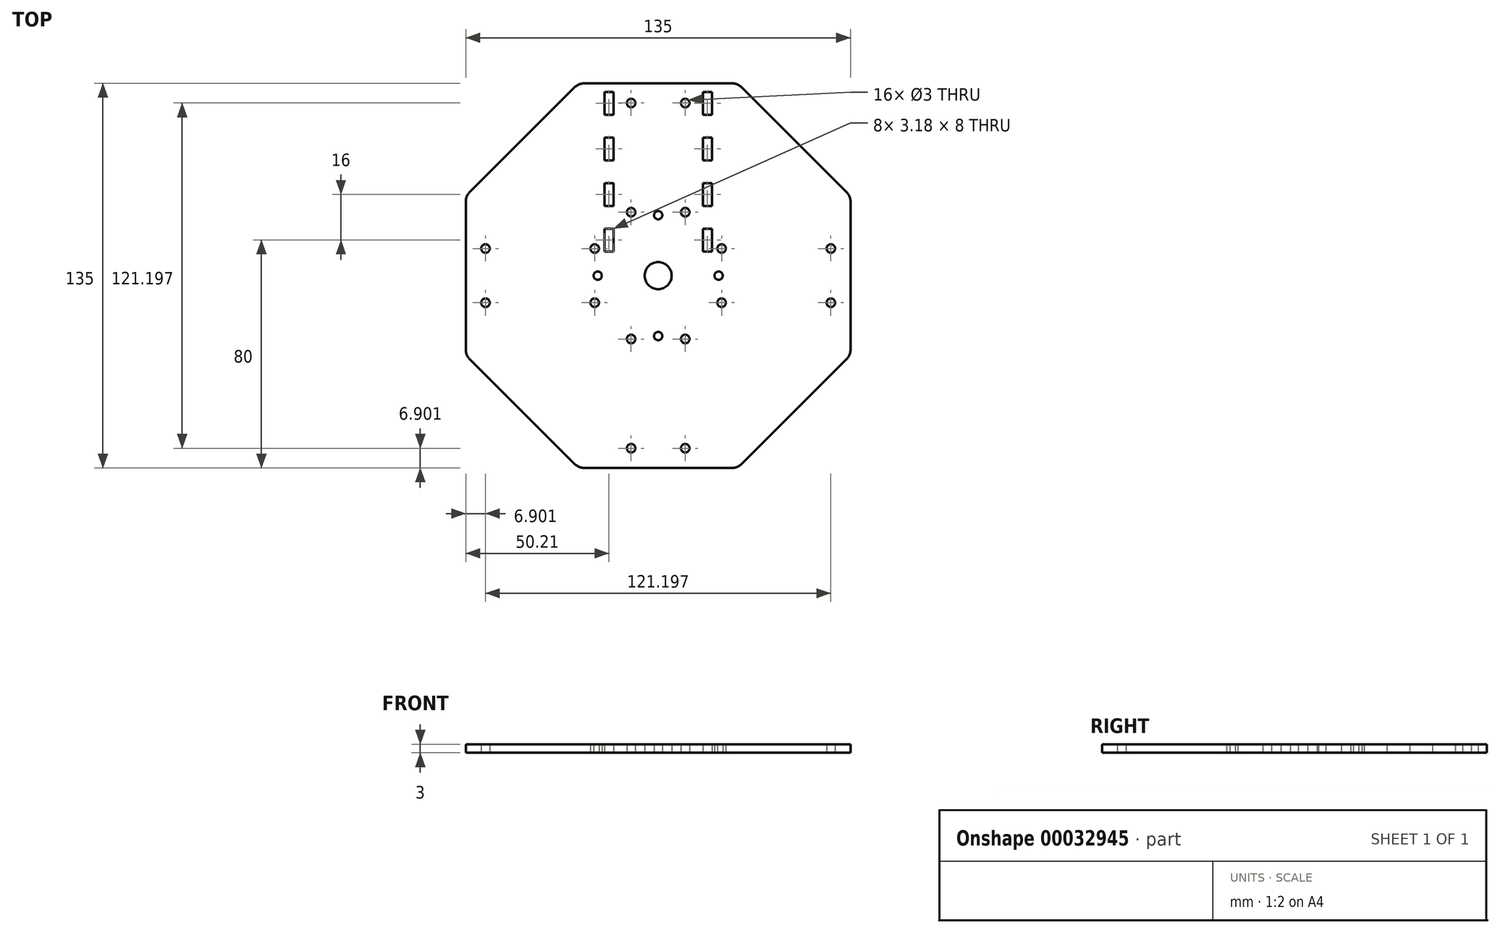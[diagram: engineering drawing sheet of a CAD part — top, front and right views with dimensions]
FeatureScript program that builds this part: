
annotation { "Feature Type Name" : "Feature", "Feature Type Description" : "" }
export const myFeature = defineFeature(function(context is Context, id is Id, definition is map)
    precondition{}
    {
        {
            var Q0;
            Q0=qCreatedBy(makeId("Top.planeOp"),FACE);
            var sketch = newSketch(context, id + "F0", { "sketchPlane" : qUnion([Q0])});
            skPoint(sketch, "E0.rect.middle", {"position": v(0, 0) * mm});
            skLineSegment(sketch, "E1", {"start": v(0, 67.5) * mm, "end": v(0, -67.5) * mm, "construction": true});
            skLineSegment(sketch, "E2", {"start": v(-67.5, 0) * mm, "end": v(67.5, 0) * mm, "construction": true});
            skLineSegment(sketch, "E3.rect.bottom", {"start": v(14, -14) * mm, "end": v(-14, -14) * mm, "construction": true});
            skLineSegment(sketch, "E3.rect.top", {"start": v(14, 14) * mm, "end": v(-14, 14) * mm, "construction": true});
            skLineSegment(sketch, "E3.rect.left", {"start": v(14, -14) * mm, "end": v(14, 14) * mm, "construction": true});
            skLineSegment(sketch, "E3.rect.right", {"start": v(-14, -14) * mm, "end": v(-14, 14) * mm, "construction": true});
            skLineSegment(sketch, "E4.rect.bottom", {"start": v(5, -5) * mm, "end": v(-5, -5) * mm, "construction": true});
            skLineSegment(sketch, "E4.rect.top", {"start": v(5, 5) * mm, "end": v(-5, 5) * mm, "construction": true});
            skLineSegment(sketch, "E4.rect.left", {"start": v(5, -5) * mm, "end": v(5, 5) * mm, "construction": true});
            skLineSegment(sketch, "E4.rect.right", {"start": v(-5, -5) * mm, "end": v(-5, 5) * mm, "construction": true});
            skLineSegment(sketch, "E5.bottom", {"start": v(-14, 14) * mm, "end": v(14, 14) * mm, "construction": true});
            skLineSegment(sketch, "E5.top", {"start": v(-14, 23) * mm, "end": v(14, 23) * mm, "construction": true});
            skLineSegment(sketch, "E5.left", {"start": v(-14, 14) * mm, "end": v(-14, 23) * mm, "construction": true});
            skLineSegment(sketch, "E5.right", {"start": v(14, 14) * mm, "end": v(14, 23) * mm, "construction": true});
            skLineSegment(sketch, "E6", {"start": v(5, 23) * mm, "end": v(5, 14) * mm, "construction": true});
            skLineSegment(sketch, "E7", {"start": v(14, 18.5) * mm, "end": v(5, 18.5) * mm, "construction": true});
            skCircle(sketch, "E8", {"center": v(0, 0) * mm, "radius": 20.8 * mm, "construction": true});
            skLineSegment(sketch, "E9", {"start": v(0, 0) * mm, "end": v(14, 14) * mm, "construction": true});
            skLineSegment(sketch, "E10", {"start": v(0, 0) * mm, "end": v(-14, 14) * mm, "construction": true});
            skCircle(sketch, "E11", {"center": v(9.5, 60.6) * mm, "radius": 1.5 * mm});
            skCircle(sketch, "E12.MirrorC", {"center": v(-9.5, 60.6) * mm, "radius": 1.5 * mm});
            skCircle(sketch, "E13.MirrorC", {"center": v(-9.5, -60.6) * mm, "radius": 1.5 * mm});
            skCircle(sketch, "E14.MirrorC", {"center": v(9.5, -60.6) * mm, "radius": 1.5 * mm});
            skCircle(sketch, "E15.MirrorC", {"center": v(60.6, -9.5) * mm, "radius": 1.5 * mm});
            skCircle(sketch, "E16.MirrorC", {"center": v(60.6, 9.5) * mm, "radius": 1.5 * mm});
            skCircle(sketch, "E17.MirrorC", {"center": v(-60.6, -9.5) * mm, "radius": 1.5 * mm});
            skCircle(sketch, "E18.MirrorC", {"center": v(-60.6, 9.5) * mm, "radius": 1.5 * mm});
            skLineSegment(sketch, "E19", {"start": v(0, 0) * mm, "end": v(95.46, 0) * mm, "construction": true});
            skLineSegment(sketch, "E20.MirrorCS", {"start": v(0, 0) * mm, "end": v(0, 95.46) * mm, "construction": true});
            skLineSegment(sketch, "E21", {"start": v(27.96, 67.5) * mm, "end": v(67.5, 27.96) * mm});
            skLineSegment(sketch, "E22.MirrorCS", {"start": v(-67.5, -27.96) * mm, "end": v(-27.96, -67.5) * mm});
            skLineSegment(sketch, "E23.MirrorCS", {"start": v(-27.96, 67.5) * mm, "end": v(-67.5, 27.96) * mm});
            skLineSegment(sketch, "E24.MirrorCS", {"start": v(27.96, -67.5) * mm, "end": v(67.5, -27.96) * mm});
            skLineSegment(sketch, "E25", {"start": v(67.5, -27.96) * mm, "end": v(67.5, 27.96) * mm});
            skLineSegment(sketch, "E26.MirrorCS", {"start": v(-67.5, -27.96) * mm, "end": v(-67.5, 27.96) * mm});
            skLineSegment(sketch, "E27.MirrorCS", {"start": v(-27.96, 67.5) * mm, "end": v(27.96, 67.5) * mm});
            skLineSegment(sketch, "E28.MirrorCS", {"start": v(27.96, -67.5) * mm, "end": v(-27.96, -67.5) * mm});
            skPoint(sketch, "E29.orphan", {"position": v(0, 95.46) * mm});
            skPoint(sketch, "E30.orphan", {"position": v(95.46, 0) * mm});
            skPoint(sketch, "E31.orphan", {"position": v(0, -95.46) * mm});
            skPoint(sketch, "E32.orphan", {"position": v(-95.46, 0) * mm});
            skCircle(sketch, "E33", {"center": v(0, 0) * mm, "radius": 4.75 * mm});
            skCircle(sketch, "E34", {"center": v(0, 21.21) * mm, "radius": 1.45 * mm});
            skCircle(sketch, "E35.1.0", {"center": v(-21.21, 0) * mm, "radius": 1.45 * mm});
            skCircle(sketch, "E35.2.0", {"center": v(0, -21.21) * mm, "radius": 1.45 * mm});
            skCircle(sketch, "E35.3.0", {"center": v(21.21, 0) * mm, "radius": 1.45 * mm});
            skLineSegment(sketch, "E36", {"start": v(-9.5, 60.6) * mm, "end": v(-9.5, 12.4) * mm, "construction": true});
            skLineSegment(sketch, "E37", {"start": v(15.7, 64.5) * mm, "end": v(15.7, 0) * mm, "construction": true});
            skLineSegment(sketch, "E38", {"start": v(-9.5, 36.5) * mm, "end": v(15.7, 36.5) * mm, "construction": true});
            skLineSegment(sketch, "E39.top", {"start": v(15.7, 64.5) * mm, "end": v(18.88, 64.5) * mm});
            skLineSegment(sketch, "E39.left", {"start": v(15.7, 56.5) * mm, "end": v(15.7, 64.5) * mm});
            skLineSegment(sketch, "E40", {"start": v(15.7, 56.5) * mm, "end": v(18.88, 56.5) * mm});
            skPoint(sketch, "E40.endSnap0", {"position": v(18.88, 50.5) * mm});
            skLineSegment(sketch, "E41.trimOffspring", {"start": v(18.88, 56.5) * mm, "end": v(18.88, 64.5) * mm});
            skPoint(sketch, "E39.bottom.end.orphan", {"position": v(18.88, 36.5) * mm});
            skLineSegment(sketch, "E42.0.1.0", {"start": v(15.7, 40.5) * mm, "end": v(15.7, 48.5) * mm});
            skLineSegment(sketch, "E42.0.1.1", {"start": v(15.7, 48.5) * mm, "end": v(18.88, 48.5) * mm});
            skLineSegment(sketch, "E42.0.1.2", {"start": v(18.88, 40.5) * mm, "end": v(18.88, 48.5) * mm});
            skLineSegment(sketch, "E42.0.1.3", {"start": v(15.7, 40.5) * mm, "end": v(18.88, 40.5) * mm});
            skLineSegment(sketch, "E42.0.2.0", {"start": v(15.7, 24.5) * mm, "end": v(15.7, 32.5) * mm});
            skLineSegment(sketch, "E42.0.2.1", {"start": v(15.7, 32.5) * mm, "end": v(18.88, 32.5) * mm});
            skLineSegment(sketch, "E42.0.2.2", {"start": v(18.88, 24.5) * mm, "end": v(18.88, 32.5) * mm});
            skLineSegment(sketch, "E42.0.2.3", {"start": v(15.7, 24.5) * mm, "end": v(18.88, 24.5) * mm});
            skLineSegment(sketch, "E42.0.3.0", {"start": v(15.7, 8.5) * mm, "end": v(15.7, 16.5) * mm});
            skLineSegment(sketch, "E42.0.3.1", {"start": v(15.7, 16.5) * mm, "end": v(18.88, 16.5) * mm});
            skLineSegment(sketch, "E42.0.3.2", {"start": v(18.88, 8.5) * mm, "end": v(18.88, 16.5) * mm});
            skLineSegment(sketch, "E42.0.3.3", {"start": v(15.7, 8.5) * mm, "end": v(18.88, 8.5) * mm});
            skLineSegment(sketch, "E42.direction1", {"start": v(15.7, 56.5) * mm, "end": v(40.7, 56.5) * mm, "construction": true});
            skLineSegment(sketch, "E42.direction2", {"start": v(15.7, 56.5) * mm, "end": v(15.7, 40.5) * mm, "construction": true});
            skCircle(sketch, "E43", {"center": v(0, 0) * mm, "radius": 27 * mm, "construction": true});
            skLineSegment(sketch, "E44", {"start": v(11.07, 9.5) * mm, "end": v(43.15, 9.5) * mm, "construction": true});
            skCircle(sketch, "E45", {"center": v(22.27, 9.5) * mm, "radius": 1.5 * mm});
            skCircle(sketch, "E46.MirrorC", {"center": v(22.27, -9.5) * mm, "radius": 1.5 * mm});
            skCircle(sketch, "E47.MirrorC", {"center": v(9.5, 22.27) * mm, "radius": 1.5 * mm});
            skCircle(sketch, "E48.MirrorC", {"center": v(-9.5, 22.27) * mm, "radius": 1.5 * mm});
            skCircle(sketch, "E49.MirrorC", {"center": v(-9.5, -22.27) * mm, "radius": 1.5 * mm});
            skCircle(sketch, "E50.MirrorC", {"center": v(9.5, -22.27) * mm, "radius": 1.5 * mm});
            skCircle(sketch, "E51.MirrorC", {"center": v(-22.27, 9.5) * mm, "radius": 1.5 * mm});
            skCircle(sketch, "E52.MirrorC", {"center": v(-22.27, -9.5) * mm, "radius": 1.5 * mm});
            skLineSegment(sketch, "E53.MirrorCS", {"start": v(-15.7, 64.5) * mm, "end": v(-18.88, 64.5) * mm});
            skLineSegment(sketch, "E54.MirrorCS", {"start": v(-15.7, 56.5) * mm, "end": v(-15.7, 64.5) * mm});
            skLineSegment(sketch, "E55.MirrorCS", {"start": v(-18.88, 56.5) * mm, "end": v(-18.88, 64.5) * mm});
            skLineSegment(sketch, "E56.MirrorCS", {"start": v(-15.7, 56.5) * mm, "end": v(-18.88, 56.5) * mm});
            skLineSegment(sketch, "E57.MirrorCS", {"start": v(-15.7, 48.5) * mm, "end": v(-18.88, 48.5) * mm});
            skLineSegment(sketch, "E58.MirrorCS", {"start": v(-15.7, 40.5) * mm, "end": v(-15.7, 48.5) * mm});
            skLineSegment(sketch, "E59.MirrorCS", {"start": v(-15.7, 40.5) * mm, "end": v(-18.88, 40.5) * mm});
            skLineSegment(sketch, "E60.MirrorCS", {"start": v(-18.88, 40.5) * mm, "end": v(-18.88, 48.5) * mm});
            skLineSegment(sketch, "E61.MirrorCS", {"start": v(-15.7, 32.5) * mm, "end": v(-18.88, 32.5) * mm});
            skLineSegment(sketch, "E62.MirrorCS", {"start": v(-15.7, 24.5) * mm, "end": v(-15.7, 32.5) * mm});
            skLineSegment(sketch, "E63.MirrorCS", {"start": v(-15.7, 24.5) * mm, "end": v(-18.88, 24.5) * mm});
            skLineSegment(sketch, "E64.MirrorCS", {"start": v(-18.88, 24.5) * mm, "end": v(-18.88, 32.5) * mm});
            skLineSegment(sketch, "E65.MirrorCS", {"start": v(-15.7, 16.5) * mm, "end": v(-18.88, 16.5) * mm});
            skLineSegment(sketch, "E66.MirrorCS", {"start": v(-15.7, 8.5) * mm, "end": v(-15.7, 16.5) * mm});
            skLineSegment(sketch, "E67.MirrorCS", {"start": v(-15.7, 8.5) * mm, "end": v(-18.88, 8.5) * mm});
            skLineSegment(sketch, "E68.MirrorCS", {"start": v(-18.88, 8.5) * mm, "end": v(-18.88, 16.5) * mm});
            skSolve(sketch);
        }
        {
            var Q0;
            Q0=qSketchRegion(id+"F0",true);
            extrude(context, id + "F1", {"entities" : qUnion([Q0]), "depth" : 3 * mm});
        }
        {
            var Q0;
            Q0=makeQuery(id+"F1.opExtrude","SWEPT_EDGE",EDGE,{"disambiguationData":[OSD([sQuery(id+"F0.wireOp",EDGE,"E23.MirrorCS"),sQuery(id+"F0.wireOp",EDGE,"E27.MirrorCS")])]});
            var Q1;
            Q1=makeQuery(id+"F1.opExtrude","SWEPT_EDGE",EDGE,{"disambiguationData":[OSD([sQuery(id+"F0.wireOp",EDGE,"E23.MirrorCS"),sQuery(id+"F0.wireOp",EDGE,"E26.MirrorCS")])]});
            var Q2;
            Q2=makeQuery(id+"F1.opExtrude","SWEPT_EDGE",EDGE,{"disambiguationData":[OSD([sQuery(id+"F0.wireOp",EDGE,"E22.MirrorCS"),sQuery(id+"F0.wireOp",EDGE,"E26.MirrorCS")])]});
            var Q3;
            Q3=makeQuery(id+"F1.opExtrude","SWEPT_EDGE",EDGE,{"disambiguationData":[OSD([sQuery(id+"F0.wireOp",EDGE,"E22.MirrorCS"),sQuery(id+"F0.wireOp",EDGE,"E28.MirrorCS")])]});
            var Q4;
            Q4=makeQuery(id+"F1.opExtrude","SWEPT_EDGE",EDGE,{"disambiguationData":[OSD([sQuery(id+"F0.wireOp",EDGE,"E24.MirrorCS"),sQuery(id+"F0.wireOp",EDGE,"E28.MirrorCS")])]});
            var Q5;
            Q5=makeQuery(id+"F1.opExtrude","SWEPT_EDGE",EDGE,{"disambiguationData":[OSD([sQuery(id+"F0.wireOp",EDGE,"E24.MirrorCS"),sQuery(id+"F0.wireOp",EDGE,"E25")])]});
            var Q6;
            Q6=makeQuery(id+"F1.opExtrude","SWEPT_EDGE",EDGE,{"disambiguationData":[OSD([sQuery(id+"F0.wireOp",EDGE,"E21"),sQuery(id+"F0.wireOp",EDGE,"E25")])]});
            var Q7;
            Q7=makeQuery(id+"F1.opExtrude","SWEPT_EDGE",EDGE,{"disambiguationData":[OSD([sQuery(id+"F0.wireOp",EDGE,"E21"),sQuery(id+"F0.wireOp",EDGE,"E27.MirrorCS")])]});
            fillet(context, id + "F2", {"entities" : qUnion([Q0, Q1, Q2, Q3, Q4, Q5, Q6, Q7]), "radius" : 5 * mm, "tangentPropagation" : true, "allowEdgeOverflow" : false});
        }
    });
